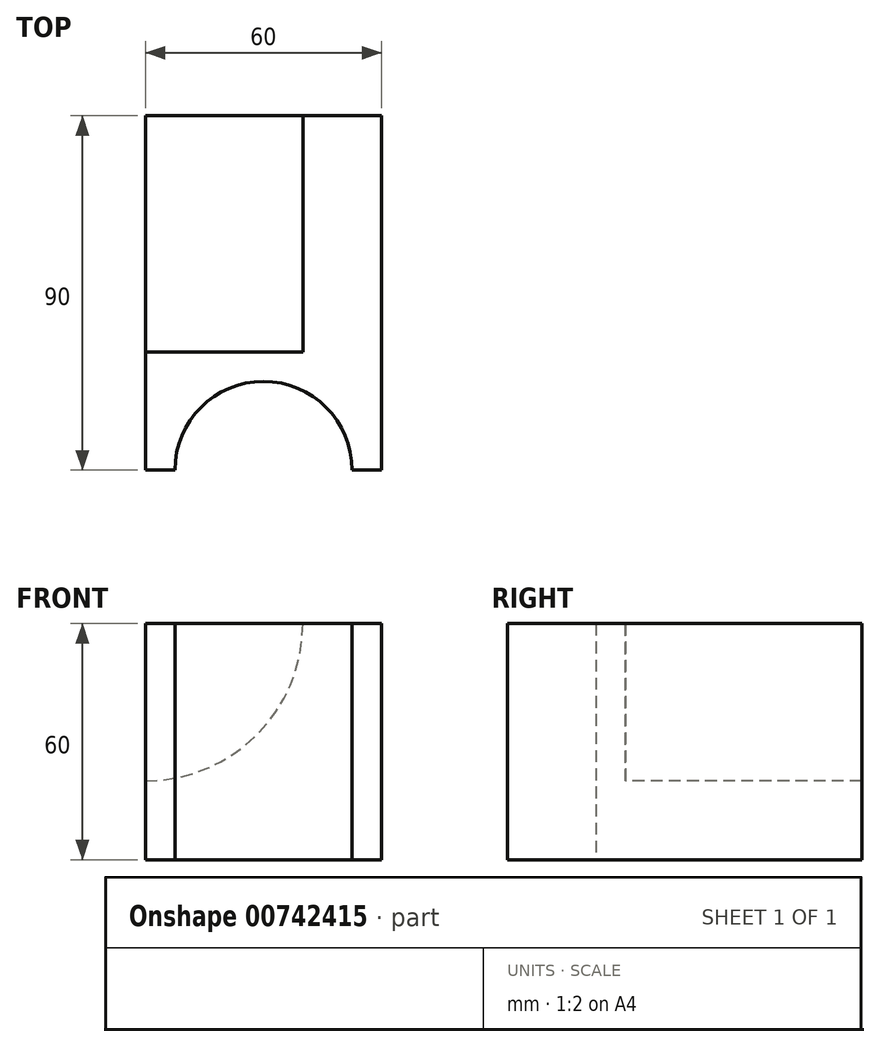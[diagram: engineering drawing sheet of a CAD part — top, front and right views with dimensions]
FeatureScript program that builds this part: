
annotation { "Feature Type Name" : "Feature", "Feature Type Description" : "" }
export const myFeature = defineFeature(function(context is Context, id is Id, definition is map)
    precondition{}
    {
        {
            var Q0;
            Q0=qCreatedBy(makeId("Top.planeOp"),FACE);
            var sketch = newSketch(context, id + "F0", { "sketchPlane" : qUnion([Q0])});
            skLineSegment(sketch, "E0", {"start": v(-30, 0) * mm, "end": v(30, 0) * mm});
            skLineSegment(sketch, "E1", {"start": v(30, 0) * mm, "end": v(30, 90) * mm});
            skLineSegment(sketch, "E2", {"start": v(30, 90) * mm, "end": v(-30, 90) * mm});
            skLineSegment(sketch, "E3", {"start": v(-30, 90) * mm, "end": v(-30, 0) * mm});
            skArc(sketch, "E4", {"start": v(22.5, 0) * mm, "mid": v(0, 22.5) * mm, "end": v(-22.5, 0) * mm});
            skSolve(sketch);
        }
        {
            var Q0;
            {var subQ0=sQuery(id+"F0.wireOp",EDGE,"E1");Q0=makeQuery(id+"F0.imprint","IMPRINT",FACE,{"disambiguationData":[TD([[makeQuery(id+"F0.imprint","IMPRINT",EDGE,{"derivedFrom":subQ0}),1.0]])]});}
            extrude(context, id + "F1", {"entities" : qUnion([Q0]), "depth" : 60 * mm, "offsetDistance" : 25 * mm});
        }
        {
            var Q0;
            Q0=qCreatedBy(makeId("Front.planeOp"),FACE);
            var sketch = newSketch(context, id + "F2", { "sketchPlane" : qUnion([Q0])});
            skLineSegment(sketch, "E5", {"start": v(-30, 0) * mm, "end": v(30, 0) * mm});
            skLineSegment(sketch, "E6", {"start": v(30, 0) * mm, "end": v(30, 60) * mm});
            skLineSegment(sketch, "E7", {"start": v(30, 60) * mm, "end": v(-30, 60) * mm});
            skLineSegment(sketch, "E8", {"start": v(-30, 60) * mm, "end": v(-30, 0) * mm});
            skArc(sketch, "E9", {"start": v(-30, 20) * mm, "mid": v(-1.72, 31.72) * mm, "end": v(10, 60) * mm});
            skSolve(sketch);
        }
        {
            var Q0;
            {var subQ3=sQuery(id+"F2.wireOp",EDGE,"E9");Q0=makeQuery(id+"F2.imprint","IMPRINT",FACE,{"disambiguationData":[TD([[makeQuery(id+"F2.imprint","IMPRINT",EDGE,{"derivedFrom":subQ3}),1.0]])]});}
            extrude(context, id + "F3", {"entities" : qUnion([Q0]), "operationType" : NewBodyOperationType.REMOVE, "oppositeDirection" : true, "depth" : 90 * mm, "offsetDistance" : 25 * mm, "hasSecondDirection" : true, "secondDirectionOppositeDirection" : true, "secondDirectionDepth" : 30 * mm});
        }
    });
